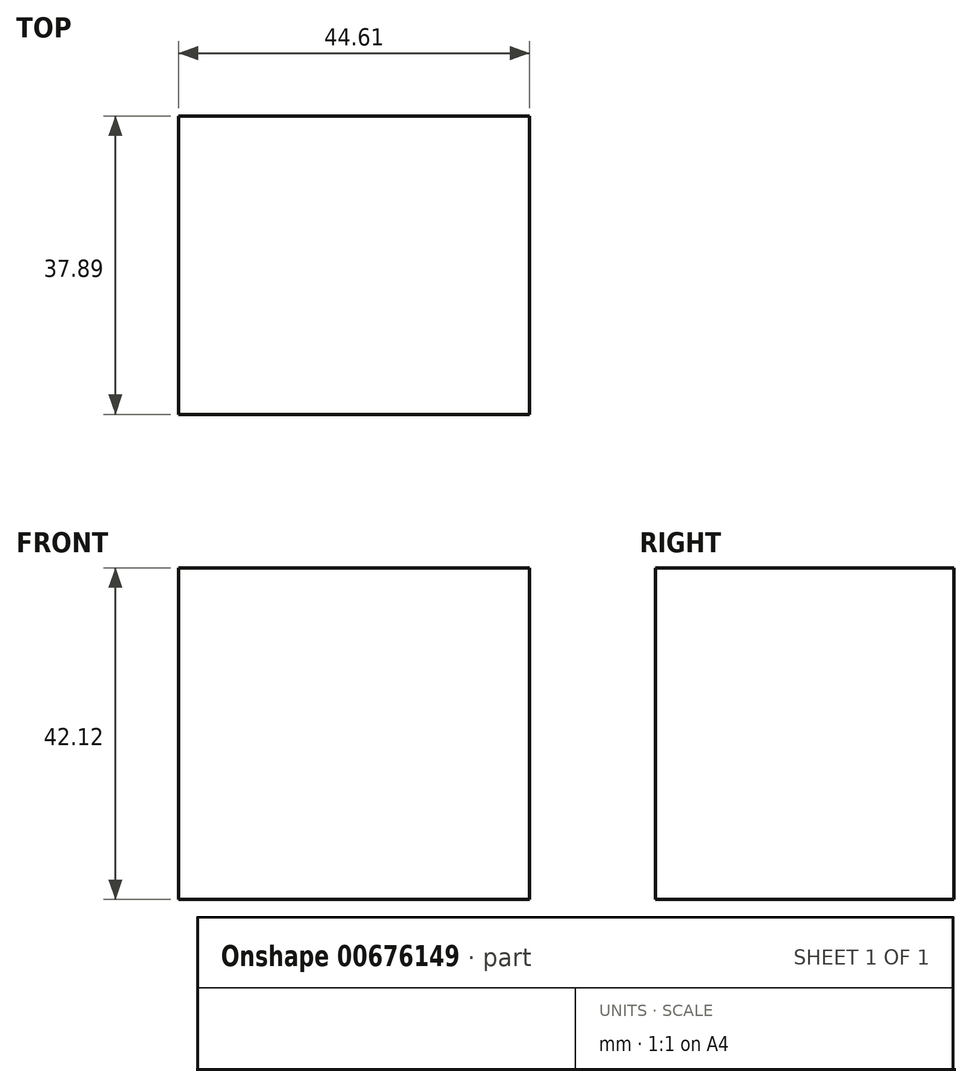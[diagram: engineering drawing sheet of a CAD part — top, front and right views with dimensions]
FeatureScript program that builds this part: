
annotation { "Feature Type Name" : "Feature", "Feature Type Description" : "" }
export const myFeature = defineFeature(function(context is Context, id is Id, definition is map)
    precondition{}
    {
        {
            var Q0;
            Q0=qCreatedBy(makeId("Right.planeOp"),FACE);
            var sketch = newSketch(context, id + "F0", { "sketchPlane" : qUnion([Q0])});
            skLineSegment(sketch, "E0", {"start": v(-37.9, 0) * mm, "end": v(-37.9, 42.12) * mm});
            skLineSegment(sketch, "E1", {"start": v(-37.9, 42.12) * mm, "end": v(0, 42.12) * mm});
            skLineSegment(sketch, "E2", {"start": v(0, 42.12) * mm, "end": v(0, 0) * mm});
            skLineSegment(sketch, "E3", {"start": v(0, 0) * mm, "end": v(-37.9, 0) * mm});
            skSolve(sketch);
        }
        {
            var Q0;
            Q0=makeQuery(id+"F0.imprint","IMPRINT",FACE,{"disambiguationData":[TD([[makeQuery(id+"F0.imprint","IMPRINT",EDGE,{"derivedFrom":sQuery(id+"F0.wireOp",EDGE,"E0")}),-1.0]])]});
            extrude(context, id + "F1", {"entities" : qUnion([Q0]), "depth" : 44.6 * mm, "offsetDistance" : 25.4 * mm});
        }
    });
